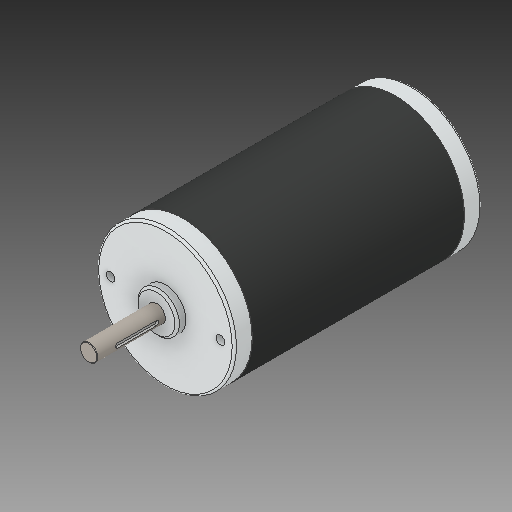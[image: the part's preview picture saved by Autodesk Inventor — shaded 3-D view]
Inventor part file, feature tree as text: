
AUTODESK INVENTOR PART (.ipt)
format: ipt  version: 2017 SP1 (Build 210196100, 196)  size: 166,912 bytes
history: native  units: in
note: dims shown in document units (in); Inventor stores cm internally (conversion verified against a paired STEP export)
features: fillet x1
ambient origin geometry x8: Origin, YZ Plane, XZ Plane, XY Plane, X Axis, Y Axis, Z Axis, Center Point
bodies: Solid1 (feature_tree)
feature tree (1):
  fillet  "Fillet5"  [1 undecoded]
note: 1 required parameter value undecoded (feature->parameter linkage not recoverable at this tier; creation-order binding heuristic only, values carry confidence <= 0.55)
